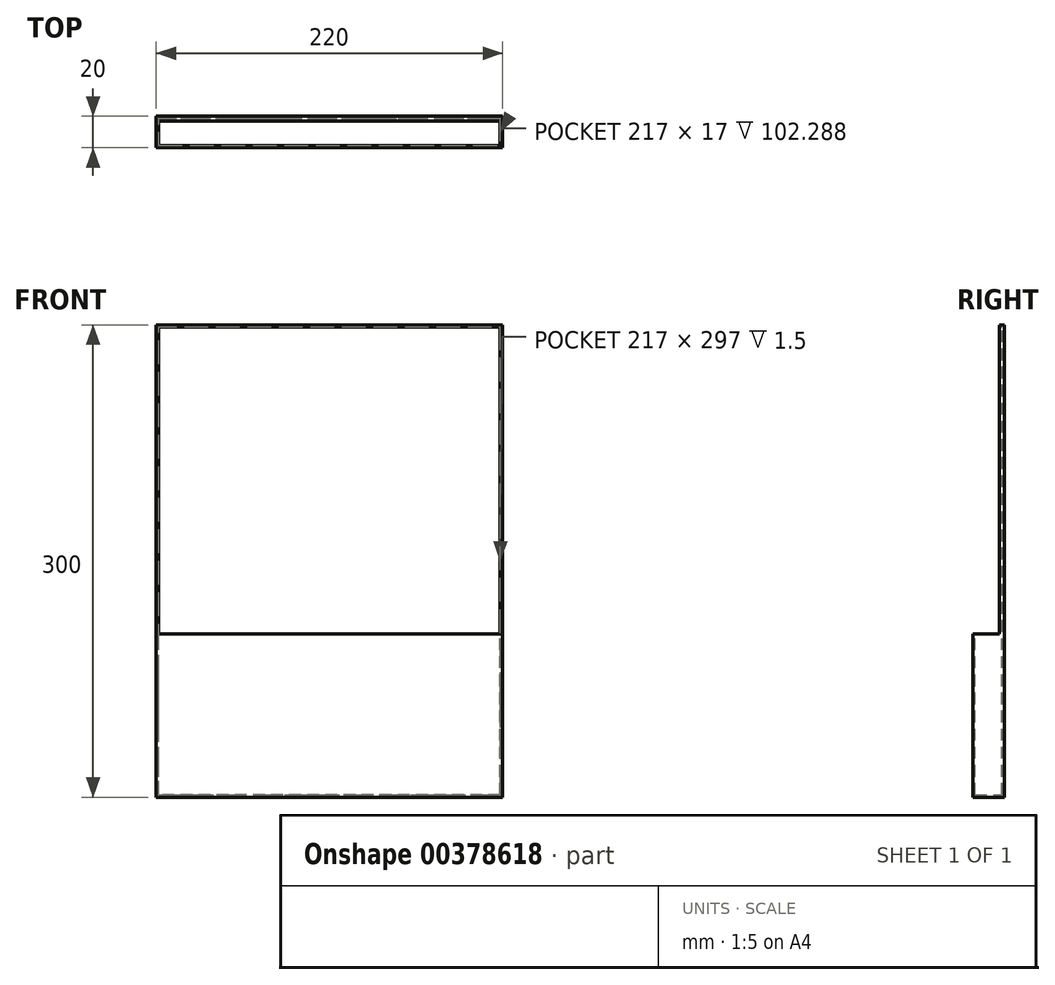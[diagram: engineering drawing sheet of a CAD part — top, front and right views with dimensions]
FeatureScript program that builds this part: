
annotation { "Feature Type Name" : "Feature", "Feature Type Description" : "" }
export const myFeature = defineFeature(function(context is Context, id is Id, definition is map)
    precondition{}
    {
        {
            var Q0;
            Q0=qCreatedBy(makeId("Front.planeOp"),FACE);
            var sketch = newSketch(context, id + "F0", { "sketchPlane" : qUnion([Q0])});
            skLineSegment(sketch, "E0.bottom", {"start": v(110, -150) * mm, "end": v(-110, -150) * mm});
            skLineSegment(sketch, "E0.top", {"start": v(110, 150) * mm, "end": v(-110, 150) * mm});
            skLineSegment(sketch, "E0.left", {"start": v(110, -150) * mm, "end": v(110, 150) * mm});
            skLineSegment(sketch, "E0.right", {"start": v(-110, -150) * mm, "end": v(-110, 150) * mm});
            skPoint(sketch, "E0.middle", {"position": v(0, 0) * mm});
            skLineSegment(sketch, "E1", {"start": v(-110, -46.21) * mm, "end": v(110, -46.21) * mm});
            skSolve(sketch);
        }
        {
            var Q0;
            {var subQ0=sQuery(id+"F0.wireOp",EDGE,"E0.bottom");Q0=makeQuery(id+"F0.imprint","IMPRINT",FACE,{"disambiguationData":[TD([[makeQuery(id+"F0.imprint","IMPRINT",EDGE,{"derivedFrom":subQ0}),-1.0]])]});}
            extrude(context, id + "F1", {"entities" : qUnion([Q0]), "depth" : 20 * mm});
        }
        {
            var Q0;
            {var subQ0=sQuery(id+"F0.wireOp",EDGE,"E0.top");Q0=makeQuery(id+"F0.imprint","IMPRINT",FACE,{"disambiguationData":[TD([[makeQuery(id+"F0.imprint","IMPRINT",EDGE,{"derivedFrom":subQ0}),1.0]])]});}
            extrude(context, id + "F2", {"entities" : qUnion([Q0]), "operationType" : NewBodyOperationType.ADD, "depth" : 3 * mm});
        }
        {
            var Q0;
            Q0=makeQuery(id+"F1.opExtrude","SWEPT_FACE",FACE,{"disambiguationData":[OSD([sQuery(id+"F0.wireOp",EDGE,"E1")])]});
            var Q1;
            Q1=makeQuery(id+"F2.opExtrude","CAP_FACE",FACE,{"disambiguationData":[OSD([sQuery(id+"F0.wireOp",EDGE,"E0.top"),sQuery(id+"F0.wireOp",EDGE,"E0.left"),sQuery(id+"F0.wireOp",EDGE,"E0.right"),sQuery(id+"F0.wireOp",EDGE,"E1")])],"isStart":false});
            shell(context, id + "F3", {"entities" : qUnion([Q0, Q1]), "thickness" : 1.5 * mm});
        }
    });
